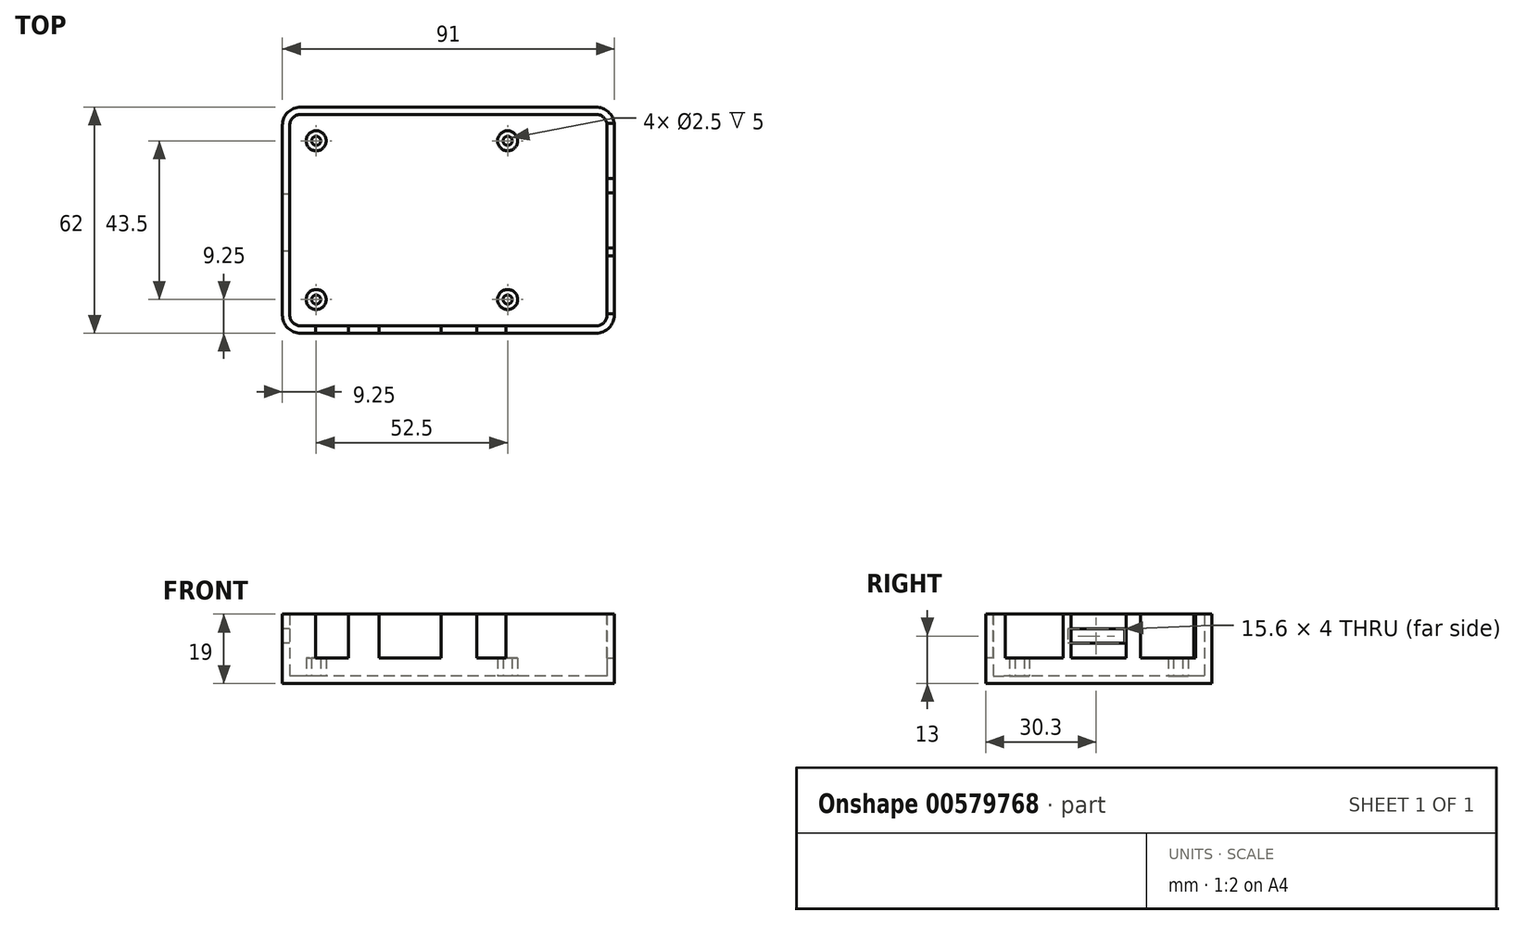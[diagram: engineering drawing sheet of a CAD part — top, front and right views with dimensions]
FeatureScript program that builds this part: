
annotation { "Feature Type Name" : "Feature", "Feature Type Description" : "" }
export const myFeature = defineFeature(function(context is Context, id is Id, definition is map)
    precondition{}
    {
        {
            var Q0;
            Q0=qCreatedBy(makeId("Top.planeOp"),FACE);
            var sketch = newSketch(context, id + "F0", { "sketchPlane" : qUnion([Q0])});
            skLineSegment(sketch, "E0.bottom", {"start": v(5, 0) * mm, "end": v(86, 0) * mm});
            skLineSegment(sketch, "E0.top", {"start": v(5, 62) * mm, "end": v(86, 62) * mm});
            skLineSegment(sketch, "E0.left", {"start": v(0, 5) * mm, "end": v(0, 57) * mm});
            skLineSegment(sketch, "E0.right", {"start": v(91, 5) * mm, "end": v(91, 57) * mm});
            skPoint(sketch, "E1.visualSharp", {"position": v(0, 62) * mm});
            skArc(sketch, "E1.filletArc", {"start": v(5, 62) * mm, "mid": v(1.46, 60.54) * mm, "end": v(0, 57) * mm});
            skPoint(sketch, "E2.visualSharp", {"position": v(91, 62) * mm});
            skArc(sketch, "E2.filletArc", {"start": v(91, 57) * mm, "mid": v(89.54, 60.54) * mm, "end": v(86, 62) * mm});
            skPoint(sketch, "E3.visualSharp", {"position": v(91, 0) * mm});
            skArc(sketch, "E3.filletArc", {"start": v(86, 0) * mm, "mid": v(89.54, 1.46) * mm, "end": v(91, 5) * mm});
            skPoint(sketch, "E4.visualSharp", {"position": v(0, 0) * mm});
            skArc(sketch, "E4.filletArc", {"start": v(0, 5) * mm, "mid": v(1.46, 1.46) * mm, "end": v(5, 0) * mm});
            skLineSegment(sketch, "E5.0", {"start": v(5, 60) * mm, "end": v(86, 60) * mm});
            skArc(sketch, "E5.1", {"start": v(89, 57) * mm, "mid": v(88.12, 59.12) * mm, "end": v(86, 60) * mm});
            skArc(sketch, "E5.2", {"start": v(5, 60) * mm, "mid": v(2.88, 59.12) * mm, "end": v(2, 57) * mm});
            skLineSegment(sketch, "E5.3", {"start": v(89, 5) * mm, "end": v(89, 57) * mm});
            skLineSegment(sketch, "E5.4", {"start": v(2, 5) * mm, "end": v(2, 57) * mm});
            skArc(sketch, "E5.5", {"start": v(2, 5) * mm, "mid": v(2.88, 2.88) * mm, "end": v(5, 2) * mm});
            skLineSegment(sketch, "E5.6", {"start": v(5, 2) * mm, "end": v(86, 2) * mm});
            skArc(sketch, "E5.7", {"start": v(86, 2) * mm, "mid": v(88.12, 2.88) * mm, "end": v(89, 5) * mm});
            skSolve(sketch);
        }
        {
            var Q0;
            Q0=makeQuery(id+"F0.imprint","IMPRINT",FACE,{"disambiguationData":[TD([[makeQuery(id+"F0.imprint","IMPRINT",EDGE,{"derivedFrom":sQuery(id+"F0.wireOp",EDGE,"E5.0")}),-1.0]])]});
            var Q1;
            Q1=makeQuery(id+"F0.imprint","IMPRINT",FACE,{"disambiguationData":[TD([[makeQuery(id+"F0.imprint","IMPRINT",EDGE,{"derivedFrom":sQuery(id+"F0.wireOp",EDGE,"E0.bottom")}),1.0]])]});
            extrude(context, id + "F1", {"entities" : qUnion([Q0, Q1]), "depth" : 2 * mm, "offsetDistance" : 25 * mm});
        }
        {
            var Q0;
            Q0 = qSketchRegion(id + "F0", true);
            extrude(context, id + "F2", {"entities" : qUnion([Q0]), "operationType" : NewBodyOperationType.ADD, "depth" : 19 * mm, "offsetDistance" : 25 * mm});
        }
        {
            var Q0;
            Q0=makeQuery(id+"F1.opExtrude","CAP_FACE",FACE,{"disambiguationData":[OSD([sQuery(id+"F0.wireOp",EDGE,"E0.bottom"),sQuery(id+"F0.wireOp",EDGE,"E0.top"),sQuery(id+"F0.wireOp",EDGE,"E0.left"),sQuery(id+"F0.wireOp",EDGE,"E0.right"),sQuery(id+"F0.wireOp",EDGE,"E1.filletArc"),sQuery(id+"F0.wireOp",EDGE,"E2.filletArc"),sQuery(id+"F0.wireOp",EDGE,"E3.filletArc"),sQuery(id+"F0.wireOp",EDGE,"E4.filletArc")])],"isStart":false});
            var sketch = newSketch(context, id + "F3", { "sketchPlane" : qUnion([Q0])});
            skCircle(sketch, "E6", {"center": v(9.25, 52.75) * mm, "radius": 2.75 * mm});
            skCircle(sketch, "E7", {"center": v(9.25, 9.25) * mm, "radius": 2.75 * mm});
            skCircle(sketch, "E8", {"center": v(61.75, 9.25) * mm, "radius": 2.75 * mm});
            skCircle(sketch, "E9", {"center": v(61.75, 52.75) * mm, "radius": 2.75 * mm});
            skCircle(sketch, "E10", {"center": v(9.25, 52.75) * mm, "radius": 1.25 * mm});
            skCircle(sketch, "E11", {"center": v(9.25, 9.25) * mm, "radius": 1.25 * mm});
            skCircle(sketch, "E12", {"center": v(61.75, 9.25) * mm, "radius": 1.25 * mm});
            skCircle(sketch, "E13", {"center": v(61.75, 52.75) * mm, "radius": 1.25 * mm});
            skSolve(sketch);
        }
        {
            var Q0;
            Q0 = qSketchRegion(id + "F3", true);
            extrude(context, id + "F4", {"entities" : qUnion([Q0]), "operationType" : NewBodyOperationType.ADD, "depth" : 5 * mm, "offsetDistance" : 25 * mm});
        }
        {
            var Q0;
            Q0=makeQuery(id+"F2.opExtrude","CAP_FACE",FACE,{"disambiguationData":[OSD([sQuery(id+"F0.wireOp",EDGE,"E0.bottom"),sQuery(id+"F0.wireOp",EDGE,"E0.top"),sQuery(id+"F0.wireOp",EDGE,"E0.left"),sQuery(id+"F0.wireOp",EDGE,"E0.right"),sQuery(id+"F0.wireOp",EDGE,"E1.filletArc"),sQuery(id+"F0.wireOp",EDGE,"E2.filletArc"),sQuery(id+"F0.wireOp",EDGE,"E3.filletArc"),sQuery(id+"F0.wireOp",EDGE,"E4.filletArc"),sQuery(id+"F0.wireOp",EDGE,"E5.0"),sQuery(id+"F0.wireOp",EDGE,"E5.1"),sQuery(id+"F0.wireOp",EDGE,"E5.2"),sQuery(id+"F0.wireOp",EDGE,"E5.3"),sQuery(id+"F0.wireOp",EDGE,"E5.4"),sQuery(id+"F0.wireOp",EDGE,"E5.5"),sQuery(id+"F0.wireOp",EDGE,"E5.6"),sQuery(id+"F0.wireOp",EDGE,"E5.7")])],"isStart":false});
            var sketch = newSketch(context, id + "F5", { "sketchPlane" : qUnion([Q0])});
            skLineSegment(sketch, "E14", {"start": v(9.05, 2) * mm, "end": v(9.05, 0) * mm});
            skLineSegment(sketch, "E15", {"start": v(18.05, 2) * mm, "end": v(18.05, 0) * mm});
            skLineSegment(sketch, "E16", {"start": v(89, 57.5) * mm, "end": v(91, 57.5) * mm});
            skLineSegment(sketch, "E17", {"start": v(9.05, 2) * mm, "end": v(18.05, 2) * mm});
            skLineSegment(sketch, "E18", {"start": v(18.05, 0) * mm, "end": v(9.05, 0) * mm});
            skLineSegment(sketch, "E19.bottom", {"start": v(26.5, 2) * mm, "end": v(43.5, 2) * mm});
            skLineSegment(sketch, "E19.top", {"start": v(26.5, 0) * mm, "end": v(43.5, 0) * mm});
            skLineSegment(sketch, "E19.left", {"start": v(26.5, 2) * mm, "end": v(26.5, 0) * mm});
            skLineSegment(sketch, "E19.right", {"start": v(43.5, 2) * mm, "end": v(43.5, 0) * mm});
            skLineSegment(sketch, "E20.bottom", {"start": v(53.25, 2) * mm, "end": v(61.25, 2) * mm});
            skLineSegment(sketch, "E20.top", {"start": v(53.25, 0) * mm, "end": v(61.25, 0) * mm});
            skLineSegment(sketch, "E20.left", {"start": v(53.25, 2) * mm, "end": v(53.25, 0) * mm});
            skLineSegment(sketch, "E20.right", {"start": v(61.25, 2) * mm, "end": v(61.25, 0) * mm});
            skLineSegment(sketch, "E21.bottom", {"start": v(89, 5.3) * mm, "end": v(91, 5.3) * mm});
            skLineSegment(sketch, "E21.top", {"start": v(89, 21.2) * mm, "end": v(91, 21.2) * mm});
            skLineSegment(sketch, "E21.left", {"start": v(89, 5.3) * mm, "end": v(89, 21.2) * mm});
            skLineSegment(sketch, "E21.right", {"start": v(91, 5.3) * mm, "end": v(91, 21.2) * mm});
            skLineSegment(sketch, "E22", {"start": v(89, 57.5) * mm, "end": v(89, 42.4) * mm});
            skLineSegment(sketch, "E23", {"start": v(89, 42.4) * mm, "end": v(91, 42.4) * mm});
            skLineSegment(sketch, "E24", {"start": v(91, 42.4) * mm, "end": v(91, 57.5) * mm});
            skLineSegment(sketch, "E25.bottom", {"start": v(89, 38.5) * mm, "end": v(91, 38.5) * mm});
            skLineSegment(sketch, "E25.top", {"start": v(89, 23.4) * mm, "end": v(91, 23.4) * mm});
            skLineSegment(sketch, "E25.left", {"start": v(89, 38.5) * mm, "end": v(89, 23.4) * mm});
            skLineSegment(sketch, "E25.right", {"start": v(91, 38.5) * mm, "end": v(91, 23.4) * mm});
            skSolve(sketch);
        }
        {
            var Q0;
            Q0 = qSketchRegion(id + "F5", true);
            extrude(context, id + "F6", {"entities" : qUnion([Q0]), "operationType" : NewBodyOperationType.REMOVE, "oppositeDirection" : true, "depth" : 12 * mm, "offsetDistance" : 25 * mm});
        }
        {
            var Q0;
            {var subQ0=sQuery(id+"F0.wireOp",EDGE,"E0.left");Q0=makeQuery(id+"F2.boolean.opBoolean","MERGE",FACE,{"derivedFrom":[makeQuery(id+"F1.opExtrude","SWEPT_FACE",FACE,{"disambiguationData":[OSD([subQ0])]}),makeQuery(id+"F2.opExtrude","SWEPT_FACE",FACE,{"disambiguationData":[OSD([subQ0])]})]});}
            var sketch = newSketch(context, id + "F7", { "sketchPlane" : qUnion([Q0])});
            skLineSegment(sketch, "E26.bottom", {"start": v(-38.1, 15) * mm, "end": v(-22.5, 15) * mm});
            skLineSegment(sketch, "E26.top", {"start": v(-38.1, 11) * mm, "end": v(-22.5, 11) * mm});
            skLineSegment(sketch, "E26.left", {"start": v(-38.1, 15) * mm, "end": v(-38.1, 11) * mm});
            skLineSegment(sketch, "E26.right", {"start": v(-22.5, 15) * mm, "end": v(-22.5, 11) * mm});
            skSolve(sketch);
        }
        {
            var Q0;
            Q0 = qSketchRegion(id + "F7", true);
            extrude(context, id + "F8", {"entities" : qUnion([Q0]), "operationType" : NewBodyOperationType.REMOVE, "oppositeDirection" : true, "depth" : 25 * mm, "offsetDistance" : 25 * mm});
        }
    });
